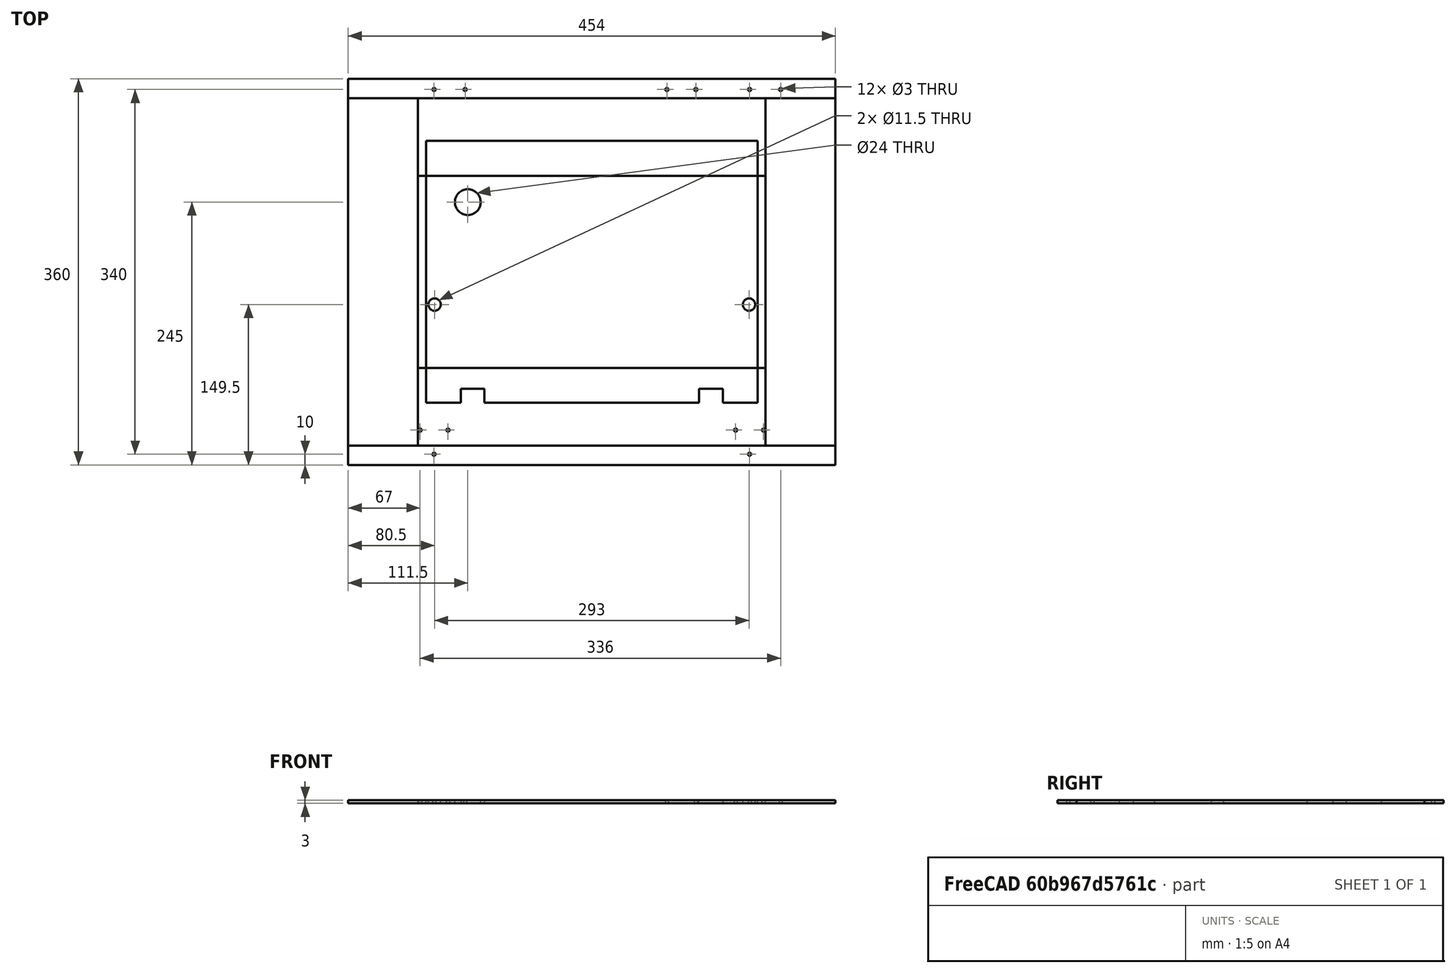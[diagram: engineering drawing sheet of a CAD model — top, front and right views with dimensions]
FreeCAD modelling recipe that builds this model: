
FCSTD DOCUMENT  (FreeCAD 0.19R24291 (Git))
Label: panel-drawing
License: Other
LicenseURL: GPL3
objects: TechDraw::DrawViewDimension×30, TechDraw::DrawViewAnnotation×9, Part::Feature×5, TechDraw::DrawSVGTemplate×5, TechDraw::DrawViewPart×5, TechDraw::DrawPage×5, Part::Part2DObjectPython×5
note: 10 computed .brp shape members not serialized (recipe doc carries the construction recipe); baked Part::Feature solids carry a one-line shape summary decoded from their .brp

FEATURE [Part::Feature] Box002001001  label="side-panel"
  shape: bbox 454 x 324 x 3 mm, 6 faces (baked)
FEATURE [Part::Feature] Cut008004003004014002002005003004003002003001003001002001002002011001007001001001001  label="rear-bottom"
  shape: bbox 309 x 244 x 3 mm, 14 faces (baked)
FEATURE [Part::Feature] Cut008004003004014002002005003004003002003001003001002001002002011001006001001001001001  label="rear-top"
  shape: bbox 324 x 179 x 3 mm, 9 faces (baked)
FEATURE [Part::Feature] Cut008004003004014002002005003004003002003001003001002001002002003004001001  label="front-panel"
  shape: bbox 454 x 360 x 3 mm, 18 faces (baked)
FEATURE [Part::Feature] Box002002001001001  label="top-panel"
  shape: bbox 324 x 324 x 3 mm, 6 faces (baked)
FEATURE [TechDraw::DrawSVGTemplate] Template
  EditableTexts = AuthorName=SnakeOil-XY; CheckDate=-; CreationDate=2022-01-24; DrawingNumber=1; FC-Scale=0.75; FC-Title=Rear-top panel; SheetNumber=1/1; Subtitle=3mm thick; SupervisorName=SnakeOil-XY; Weight=-
  Height = 297
  Orientation = 1
  Width = 420
FEATURE [TechDraw::DrawSVGTemplate] Template001
  EditableTexts = AuthorName=SnakeOil-XY; CheckDate=-; CreationDate=2022-01-24; DrawingNumber=1; FC-Scale=0.75; FC-Title=Rear-bottom panel; SheetNumber=1/1; Subtitle=3mm thick; SupervisorName=SnakeOil-XY; Weight=-
  Height = 297
  Orientation = 1
  Width = 420
FEATURE [TechDraw::DrawSVGTemplate] Template002
  EditableTexts = AuthorName=SnakeOil-XY; CheckDate=-; CreationDate=2022-01-24; DrawingNumber=1; FC-Scale=0.5; FC-Title=Top panel; SheetNumber=1/1; Subtitle=Top panel; SupervisorName=SnakeOil-XY; Weight=-
  Height = 297
  Orientation = 1
  Width = 420
FEATURE [TechDraw::DrawSVGTemplate] Template003
  EditableTexts = AuthorName=SnakeOil-XY; CheckDate=-; CreationDate=2022-01-24; DrawingNumber=1; FC-Scale=0.5; FC-Title=Side panel; SheetNumber=1/1; Subtitle=3mm; SupervisorName=SnakeOil-XY; Weight=-
  Height = 297
  Orientation = 1
  Width = 420
FEATURE [TechDraw::DrawSVGTemplate] Template004
  EditableTexts = AuthorName=SnakeOil-XY; CheckDate=-; CreationDate=2022-01-24; DrawingNumber=1; FC-Scale=0.5; FC-Title=Front panel; SheetNumber=1/1; Subtitle=3mm; SupervisorName=SnakeOil-XY; Weight=-
  Height = 297
  Orientation = 1
  Width = 420
FEATURE [TechDraw::DrawViewPart] View
  CoarseView = false
  Direction = (0,0,1)
  Focus = 100
  HardHidden = false
  IsoCount = 0
  IsoHidden = false
  IsoVisible = false
  LockPosition = false
  Perspective = false
  Rotation = 0
  Scale = 0.75
  ScaleType = 0
  SeamHidden = false
  SeamVisible = true
  SmoothHidden = false
  SmoothVisible = true
  Source = -> [Cut008004003004014002002005003004003002003001003001002001002002011001006001001001001001]
  X = 185.107
  XDirection = (1,0,0)
  Y = 185.41
FEATURE [TechDraw::DrawViewDimension] Dimension
  Arbitrary = false
  ArbitraryTolerances = false
  EqualTolerance = true
  FormatSpec = ⌀%.2f
  FormatSpecOverTolerance = %+.2f
  FormatSpecUnderTolerance = %+.2f
  Inverted = false
  LockPosition = false
  MeasureType = 1
  OverTolerance = 0
  References2D = -> [View]
  Rotation = 0
  ScaleType = 0
  TheoreticalExact = false
  Type = 5
  UnderTolerance = 0
  X = -63.1769
  Y = 37.7688
FEATURE [TechDraw::DrawViewDimension] Dimension001
  Arbitrary = false
  ArbitraryTolerances = false
  EqualTolerance = true
  FormatSpec = 2x ⌀%.2f
  FormatSpecOverTolerance = %+.2f
  FormatSpecUnderTolerance = %+.2f
  Inverted = false
  LockPosition = false
  MeasureType = 1
  OverTolerance = 0
  References2D = -> [View]
  Rotation = 0
  ScaleType = 0
  TheoreticalExact = false
  Type = 5
  UnderTolerance = 0
  X = -93.4041
  Y = -8.93294
FEATURE [TechDraw::DrawViewDimension] Dimension003
  Arbitrary = false
  ArbitraryTolerances = false
  EqualTolerance = true
  FormatSpec = %.2f
  FormatSpecOverTolerance = %+.2f
  FormatSpecUnderTolerance = %+.2f
  Inverted = false
  LockPosition = false
  MeasureType = 1
  OverTolerance = 0
  References2D = -> [View]
  Rotation = 0
  ScaleType = 0
  TheoreticalExact = false
  Type = 1
  UnderTolerance = 0
  X = -115.374
  Y = -31.5222
FEATURE [TechDraw::DrawViewDimension] Dimension005
  Arbitrary = false
  ArbitraryTolerances = false
  EqualTolerance = true
  FormatSpec = %.2f
  FormatSpecOverTolerance = %+.2f
  FormatSpecUnderTolerance = %+.2f
  Inverted = false
  LockPosition = false
  MeasureType = 1
  OverTolerance = 0
  References2D = -> [View]
  Rotation = 0
  ScaleType = 0
  TheoreticalExact = false
  Type = 2
  UnderTolerance = 0
  X = -93.2768
  Y = -42.6492
FEATURE [TechDraw::DrawViewDimension] Dimension007
  Arbitrary = false
  ArbitraryTolerances = false
  EqualTolerance = true
  FormatSpec = %.2f
  FormatSpecOverTolerance = %+.2f
  FormatSpecUnderTolerance = %+.2f
  Inverted = false
  LockPosition = false
  MeasureType = 1
  OverTolerance = 0
  References2D = -> [View]
  Rotation = 0
  ScaleType = 0
  TheoreticalExact = false
  Type = 1
  UnderTolerance = 0
  X = -102.965
  Y = 34.1163
FEATURE [TechDraw::DrawViewDimension] Dimension008
  Arbitrary = false
  ArbitraryTolerances = false
  EqualTolerance = true
  FormatSpec = %.2f
  FormatSpecOverTolerance = %+.2f
  FormatSpecUnderTolerance = %+.2f
  Inverted = false
  LockPosition = false
  MeasureType = 1
  OverTolerance = 0
  References2D = -> [View]
  Rotation = 0
  ScaleType = 0
  TheoreticalExact = false
  Type = 2
  UnderTolerance = 0
  X = -63.9426
  Y = 60.1316
FEATURE [TechDraw::DrawViewDimension] Dimension009
  Arbitrary = false
  ArbitraryTolerances = false
  EqualTolerance = true
  FormatSpec = %
  FormatSpecOverTolerance = %+.2f
  FormatSpecUnderTolerance = %+.2f
  Inverted = false
  LockPosition = false
  MeasureType = 1
  OverTolerance = 0
  References2D = -> [View]
  Rotation = 0
  ScaleType = 0
  TheoreticalExact = false
  Type = 1
  UnderTolerance = 0
  X = -2.19406
  Y = 79.8341
FEATURE [TechDraw::DrawViewDimension] Dimension010
  Arbitrary = false
  ArbitraryTolerances = false
  EqualTolerance = true
  FormatSpec = %.2f
  FormatSpecOverTolerance = %+.2f
  FormatSpecUnderTolerance = %+.2f
  Inverted = false
  LockPosition = false
  MeasureType = 1
  OverTolerance = 0
  References2D = -> [View]
  Rotation = 0
  ScaleType = 0
  TheoreticalExact = false
  Type = 2
  UnderTolerance = 0
  X = 143.441
  Y = 1.91196
FEATURE [TechDraw::DrawViewAnnotation] Annotation
  Font = osifont
  LineSpace = 80
  LockPosition = false
  MaxWidth = -1
  Rotation = 0
  ScaleType = 0
  Text = (394mm for 250 machine)
  TextSize = 5
  TextStyle = 0
  X = 219.271
  Y = 261.12
FEATURE [TechDraw::DrawPage] Page  label="rear-top-drawing"
  KeepUpdated = true
  NextBalloonIndex = 1
  ProjectionType = 0
  Template = -> Template
  Views = -> [View,Dimension,Dimension001,Dimension003,Dimension005,Dimension007,Dimension008,Dimension009,Dimension010,Annotation]
FEATURE [TechDraw::DrawViewPart] View001
  CoarseView = false
  Direction = (0,0,1)
  Focus = 100
  HardHidden = false
  IsoCount = 0
  IsoHidden = false
  IsoVisible = false
  LockPosition = false
  Perspective = false
  Rotation = 0
  Scale = 0.75
  ScaleType = 0
  SeamHidden = false
  SeamVisible = true
  SmoothHidden = false
  SmoothVisible = true
  Source = -> [Cut008004003004014002002005003004003002003001003001002001002002011001007001001001001]
  X = 164.19
  XDirection = (1,0,0)
  Y = 175.276
FEATURE [TechDraw::DrawViewDimension] Dimension011
  Arbitrary = false
  ArbitraryTolerances = false
  EqualTolerance = true
  FormatSpec = %.2f
  FormatSpecOverTolerance = %+.2f
  FormatSpecUnderTolerance = %+.2f
  Inverted = false
  LockPosition = false
  MeasureType = 1
  OverTolerance = 0
  References2D = -> [View001]
  Rotation = 0
  ScaleType = 0
  TheoreticalExact = false
  Type = 1
  UnderTolerance = 0
  X = -0.647751
  Y = 101.475
FEATURE [TechDraw::DrawViewDimension] Dimension012
  Arbitrary = false
  ArbitraryTolerances = false
  EqualTolerance = true
  FormatSpec = %.2f
  FormatSpecOverTolerance = %+.2f
  FormatSpecUnderTolerance = %+.2f
  Inverted = false
  LockPosition = false
  MeasureType = 1
  OverTolerance = 0
  References2D = -> [View001]
  Rotation = 0
  ScaleType = 0
  TheoreticalExact = false
  Type = 2
  UnderTolerance = 0
  X = 122.741
  Y = 0.12955
FEATURE [TechDraw::DrawViewDimension] Dimension013
  Arbitrary = false
  ArbitraryTolerances = false
  EqualTolerance = true
  FormatSpec = %.2f
  FormatSpecOverTolerance = %+.2f
  FormatSpecUnderTolerance = %+.2f
  Inverted = false
  LockPosition = false
  MeasureType = 1
  OverTolerance = 0
  References2D = -> [View001]
  Rotation = 0
  ScaleType = 0
  TheoreticalExact = false
  Type = 1
  UnderTolerance = 0
  X = -103.688
  Y = -91.5
FEATURE [TechDraw::DrawViewDimension] Dimension014
  Arbitrary = false
  ArbitraryTolerances = false
  EqualTolerance = true
  FormatSpec = %.2f
  FormatSpecOverTolerance = %+.2f
  FormatSpecUnderTolerance = %+.2f
  Inverted = false
  LockPosition = false
  MeasureType = 1
  OverTolerance = 0
  References2D = -> [View001]
  Rotation = 0
  ScaleType = 0
  TheoreticalExact = false
  Type = 1
  UnderTolerance = 0
  X = -83.25
  Y = -91.5
FEATURE [TechDraw::DrawViewDimension] Dimension015
  Arbitrary = false
  ArbitraryTolerances = false
  EqualTolerance = true
  FormatSpec = %.2f
  FormatSpecOverTolerance = %+.2f
  FormatSpecUnderTolerance = %+.2f
  Inverted = false
  LockPosition = false
  MeasureType = 1
  OverTolerance = 0
  References2D = -> [View001]
  Rotation = 0
  ScaleType = 0
  TheoreticalExact = false
  Type = 2
  UnderTolerance = 0
  X = -126.349
  Y = -83.6453
FEATURE [TechDraw::DrawViewAnnotation] Annotation001
  Font = osifont
  LineSpace = 80
  LockPosition = false
  MaxWidth = -1
  Rotation = 0
  ScaleType = 0
  Text = (379mm for 250 machine)
  TextSize = 5
  TextStyle = 0
  X = 199.659
  Y = 272.42
FEATURE [TechDraw::DrawViewAnnotation] Annotation002
  Font = osifont
  LineSpace = 80
  LockPosition = false
  MaxWidth = -1
  Rotation = 90
  ScaleType = 0
  Text = (294mm for 250 machine)
  TextSize = 5
  TextStyle = 0
  X = 287.979
  Y = 208.68
FEATURE [TechDraw::DrawPage] Page001  label="rear-bottom-drawing"
  KeepUpdated = true
  NextBalloonIndex = 1
  ProjectionType = 0
  Template = -> Template001
  Views = -> [View001,Dimension011,Dimension012,Dimension013,Dimension014,Dimension015,Annotation001,Annotation002]
FEATURE [TechDraw::DrawViewPart] View002
  CoarseView = false
  Direction = (0,0,1)
  Focus = 100
  HardHidden = false
  IsoCount = 0
  IsoHidden = false
  IsoVisible = false
  LockPosition = false
  Perspective = false
  Rotation = 0
  Scale = 0.5
  ScaleType = 0
  SeamHidden = false
  SeamVisible = true
  SmoothHidden = false
  SmoothVisible = true
  Source = -> [Box002002001001001]
  X = 119.638
  XDirection = (1,0,0)
  Y = 187.906
FEATURE [TechDraw::DrawViewDimension] Dimension016
  Arbitrary = false
  ArbitraryTolerances = false
  EqualTolerance = true
  FormatSpec = %.2f
  FormatSpecOverTolerance = %+.2f
  FormatSpecUnderTolerance = %+.2f
  Inverted = false
  LockPosition = false
  MeasureType = 1
  OverTolerance = 0
  References2D = -> [View002]
  Rotation = 0
  ScaleType = 0
  TheoreticalExact = false
  Type = 1
  UnderTolerance = 0
  X = -27.8551
  Y = -90.4707
FEATURE [TechDraw::DrawViewDimension] Dimension017
  Arbitrary = false
  ArbitraryTolerances = false
  EqualTolerance = true
  FormatSpec = %.2f
  FormatSpecOverTolerance = %+.2f
  FormatSpecUnderTolerance = %+.2f
  Inverted = false
  LockPosition = false
  MeasureType = 1
  OverTolerance = 0
  References2D = -> [View002]
  Rotation = 0
  ScaleType = 0
  TheoreticalExact = false
  Type = 2
  UnderTolerance = 0
  X = 97.3416
  Y = -29.3407
FEATURE [TechDraw::DrawViewAnnotation] Annotation003
  Font = osifont
  LineSpace = 80
  LockPosition = false
  MaxWidth = -1
  Rotation = 0
  ScaleType = 0
  Text = (394mm for 250 machine)
  TextSize = 5
  TextStyle = 0
  X = 127.92
  Y = 92.9756
FEATURE [TechDraw::DrawViewAnnotation] Annotation004
  Font = osifont
  LineSpace = 80
  LockPosition = false
  MaxWidth = -1
  Rotation = 90
  ScaleType = 0
  Text = (374mm for 250 machine)
  TextSize = 5
  TextStyle = 0
  X = 218.728
  Y = 192.14
FEATURE [TechDraw::DrawPage] Page002  label="top-drawing"
  KeepUpdated = true
  NextBalloonIndex = 1
  ProjectionType = 0
  Template = -> Template002
  Views = -> [View002,Dimension016,Dimension017,Annotation003,Annotation004]
FEATURE [TechDraw::DrawViewPart] View003
  CoarseView = false
  Direction = (0,0,1)
  Focus = 100
  HardHidden = false
  IsoCount = 0
  IsoHidden = false
  IsoVisible = false
  LockPosition = false
  Perspective = false
  Rotation = 0
  Scale = 0.5
  ScaleType = 0
  SeamHidden = false
  SeamVisible = true
  SmoothHidden = false
  SmoothVisible = true
  Source = -> [Box002001001]
  X = 168.552
  XDirection = (1,0,0)
  Y = 178.45
FEATURE [TechDraw::DrawViewDimension] Dimension018
  Arbitrary = false
  ArbitraryTolerances = false
  EqualTolerance = true
  FormatSpec = %.2f
  FormatSpecOverTolerance = %+.2f
  FormatSpecUnderTolerance = %+.2f
  Inverted = false
  LockPosition = false
  MeasureType = 1
  OverTolerance = 0
  References2D = -> [View003]
  Rotation = 0
  ScaleType = 0
  TheoreticalExact = false
  Type = 1
  UnderTolerance = 0
  X = -38.0811
  Y = -89.2997
FEATURE [TechDraw::DrawViewDimension] Dimension019
  Arbitrary = false
  ArbitraryTolerances = false
  EqualTolerance = true
  FormatSpec = %.2f
  FormatSpecOverTolerance = %+.2f
  FormatSpecUnderTolerance = %+.2f
  Inverted = false
  LockPosition = false
  MeasureType = 1
  OverTolerance = 0
  References2D = -> [View003]
  Rotation = 0
  ScaleType = 0
  TheoreticalExact = false
  Type = 2
  UnderTolerance = 0
  X = 121.067
  Y = -19.5288
FEATURE [TechDraw::DrawViewAnnotation] Annotation005
  Font = osifont
  LineSpace = 80
  LockPosition = false
  MaxWidth = -1
  Rotation = 0
  ScaleType = 0
  Text = (504mm for 250 machine)
  TextSize = 5
  TextStyle = 0
  X = 167.525
  Y = 84.7874
FEATURE [TechDraw::DrawViewAnnotation] Annotation006
  Font = osifont
  LineSpace = 80
  LockPosition = false
  MaxWidth = -1
  Rotation = 90
  ScaleType = 0
  Text = (374mm for 250 machine)
  TextSize = 5
  TextStyle = 0
  X = 291.777
  Y = 192.928
FEATURE [TechDraw::DrawPage] Page003  label="side-drawing"
  KeepUpdated = true
  NextBalloonIndex = 1
  ProjectionType = 0
  Template = -> Template003
  Views = -> [View003,Dimension018,Dimension019,Annotation005,Annotation006]
FEATURE [TechDraw::DrawViewPart] View004
  CoarseView = false
  Direction = (0,0,1)
  Focus = 100
  HardHidden = false
  IsoCount = 0
  IsoHidden = false
  IsoVisible = false
  LockPosition = false
  Perspective = false
  Rotation = 0
  Scale = 0.5
  ScaleType = 0
  SeamHidden = false
  SeamVisible = true
  SmoothHidden = false
  SmoothVisible = true
  Source = -> [Cut008004003004014002002005003004003002003001003001002001002002003004001001]
  X = 151.176
  XDirection = (1,0,0)
  Y = 183.76
FEATURE [TechDraw::DrawViewDimension] Dimension020
  Arbitrary = false
  ArbitraryTolerances = false
  EqualTolerance = true
  FormatSpec = %.2f
  FormatSpecOverTolerance = %+.2f
  FormatSpecUnderTolerance = %+.2f
  Inverted = false
  LockPosition = false
  MeasureType = 1
  OverTolerance = 0
  References2D = -> [View004]
  Rotation = 0
  ScaleType = 0
  TheoreticalExact = false
  Type = 1
  UnderTolerance = 0
  X = -31.6164
  Y = -105.298
FEATURE [TechDraw::DrawViewDimension] Dimension021
  Arbitrary = false
  ArbitraryTolerances = false
  EqualTolerance = true
  FormatSpec = %.2f
  FormatSpecOverTolerance = %+.2f
  FormatSpecUnderTolerance = %+.2f
  Inverted = false
  LockPosition = false
  MeasureType = 1
  OverTolerance = 0
  References2D = -> [View004]
  Rotation = 0
  ScaleType = 0
  TheoreticalExact = false
  Type = 2
  UnderTolerance = 0
  X = 121.807
  Y = -27.4284
FEATURE [TechDraw::DrawViewDimension] Dimension022
  Arbitrary = false
  ArbitraryTolerances = false
  EqualTolerance = true
  FormatSpec = %.2f
  FormatSpecOverTolerance = %+.2f
  FormatSpecUnderTolerance = %+.2f
  Inverted = false
  LockPosition = false
  MeasureType = 1
  OverTolerance = 0
  References2D = -> [View004]
  Rotation = 0
  ScaleType = 0
  TheoreticalExact = false
  Type = 1
  UnderTolerance = 0
  X = -93.5568
  Y = 101.636
FEATURE [TechDraw::DrawViewDimension] Dimension023
  Arbitrary = false
  ArbitraryTolerances = false
  EqualTolerance = true
  FormatSpec = %.2f
  FormatSpecOverTolerance = %+.2f
  FormatSpecUnderTolerance = %+.2f
  Inverted = false
  LockPosition = false
  MeasureType = 1
  OverTolerance = 0
  References2D = -> [View004]
  Rotation = 0
  ScaleType = 0
  TheoreticalExact = false
  Type = 1
  UnderTolerance = 0
  X = -65.7958
  Y = 101.577
FEATURE [TechDraw::DrawViewDimension] Dimension024
  Arbitrary = false
  ArbitraryTolerances = false
  EqualTolerance = true
  FormatSpec = %.2f
  FormatSpecOverTolerance = %+.2f
  FormatSpecUnderTolerance = %+.2f
  Inverted = false
  LockPosition = false
  MeasureType = 1
  OverTolerance = 0
  References2D = -> [View004]
  Rotation = 0
  ScaleType = 0
  TheoreticalExact = false
  Type = 1
  UnderTolerance = 0
  X = 79.383
  Y = 100.436
FEATURE [TechDraw::DrawViewDimension] Dimension025
  Arbitrary = false
  ArbitraryTolerances = false
  EqualTolerance = true
  FormatSpec = %.2f
  FormatSpecOverTolerance = %+.2f
  FormatSpecUnderTolerance = %+.2f
  Inverted = false
  LockPosition = false
  MeasureType = 1
  OverTolerance = 0
  References2D = -> [View004]
  Rotation = 0
  ScaleType = 0
  TheoreticalExact = false
  Type = 1
  UnderTolerance = 0
  X = 41.3147
  Y = 100.423
FEATURE [TechDraw::DrawViewDimension] Dimension026
  Arbitrary = false
  ArbitraryTolerances = false
  EqualTolerance = true
  FormatSpec = %.2f
  FormatSpecOverTolerance = %+.2f
  FormatSpecUnderTolerance = %+.2f
  Inverted = false
  LockPosition = false
  MeasureType = 1
  OverTolerance = 0
  References2D = -> [View004]
  Rotation = 0
  ScaleType = 0
  TheoreticalExact = false
  Type = 2
  UnderTolerance = 0
  X = -129.096
  Y = 89.8844
FEATURE [TechDraw::DrawViewDimension] Dimension027
  Arbitrary = false
  ArbitraryTolerances = false
  EqualTolerance = true
  FormatSpec = %.2f
  FormatSpecOverTolerance = %+.2f
  FormatSpecUnderTolerance = %+.2f
  Inverted = false
  LockPosition = false
  MeasureType = 1
  OverTolerance = 0
  References2D = -> [View004]
  Rotation = 0
  ScaleType = 0
  TheoreticalExact = false
  Type = 1
  UnderTolerance = 0
  X = -96.3022
  Y = -61.0088
FEATURE [TechDraw::DrawViewDimension] Dimension028
  Arbitrary = false
  ArbitraryTolerances = false
  EqualTolerance = true
  FormatSpec = %.2f
  FormatSpecOverTolerance = %+.2f
  FormatSpecUnderTolerance = %+.2f
  Inverted = false
  LockPosition = false
  MeasureType = 1
  OverTolerance = 0
  References2D = -> [View004]
  Rotation = 0
  ScaleType = 0
  TheoreticalExact = false
  Type = 1
  UnderTolerance = 0
  X = -96.2754
  Y = -91.6838
FEATURE [TechDraw::DrawViewDimension] Dimension029
  Arbitrary = false
  ArbitraryTolerances = false
  EqualTolerance = true
  FormatSpec = %.2f
  FormatSpecOverTolerance = %+.2f
  FormatSpecUnderTolerance = %+.2f
  Inverted = false
  LockPosition = false
  MeasureType = 1
  OverTolerance = 0
  References2D = -> [View004]
  Rotation = 0
  ScaleType = 0
  TheoreticalExact = false
  Type = 1
  UnderTolerance = 0
  X = -90.4931
  Y = -99.587
FEATURE [TechDraw::DrawViewDimension] Dimension030
  Arbitrary = false
  ArbitraryTolerances = false
  EqualTolerance = true
  FormatSpec = %.2f
  FormatSpecOverTolerance = %+.2f
  FormatSpecUnderTolerance = %+.2f
  Inverted = false
  LockPosition = false
  MeasureType = 1
  OverTolerance = 0
  References2D = -> [View004]
  Rotation = 0
  ScaleType = 0
  TheoreticalExact = false
  Type = 2
  UnderTolerance = 0
  X = -58.819
  Y = -76.9697
FEATURE [TechDraw::DrawViewDimension] Dimension031
  Arbitrary = false
  ArbitraryTolerances = false
  EqualTolerance = true
  FormatSpec = %.2f
  FormatSpecOverTolerance = %+.2f
  FormatSpecUnderTolerance = %+.2f
  Inverted = false
  LockPosition = false
  MeasureType = 1
  OverTolerance = 0
  References2D = -> [View004]
  Rotation = 0
  ScaleType = 0
  TheoreticalExact = false
  Type = 2
  UnderTolerance = 0
  X = -50.4742
  Y = -59.6006
FEATURE [TechDraw::DrawViewDimension] Dimension032
  Arbitrary = false
  ArbitraryTolerances = false
  EqualTolerance = true
  FormatSpec = 12x ⌀%.2f
  FormatSpecOverTolerance = %+.2f
  FormatSpecUnderTolerance = %+.2f
  Inverted = false
  LockPosition = false
  MeasureType = 1
  OverTolerance = 0
  References2D = -> [View004]
  Rotation = 0
  ScaleType = 0
  TheoreticalExact = false
  Type = 5
  UnderTolerance = 0
  X = 38.1332
  Y = -54.992
FEATURE [TechDraw::DrawViewAnnotation] Annotation007
  Font = osifont
  LineSpace = 80
  LockPosition = false
  MaxWidth = -1
  Rotation = 90
  ScaleType = 0
  Text = (430mm for 250 machine)
  TextSize = 5
  TextStyle = 0
  X = 275.299
  Y = 189.185
FEATURE [TechDraw::DrawViewAnnotation] Annotation008
  Font = osifont
  LineSpace = 80
  LockPosition = false
  MaxWidth = -1
  Rotation = 0
  ScaleType = 0
  Text = (504mm for 250 machine)
  TextSize = 5
  TextStyle = 0
  X = 155.686
  Y = 74.25
FEATURE [TechDraw::DrawPage] Page004  label="front-drawing"
  KeepUpdated = true
  NextBalloonIndex = 1
  ProjectionType = 0
  Template = -> Template004
  Views = -> [View004,Dimension020,Dimension021,Dimension022,Dimension023,Dimension024,Dimension025,Dimension026,Dimension027,Dimension028,Dimension029,Dimension030,Dimension031,Dimension032,Annotation007,Annotation008]
FEATURE [Part::Part2DObjectPython] Shape2DView  label="side-panel-2d"  # Draft 2D object (typed FeaturePython)
  Base = -> Box002001001
  FuseArch = false
  HiddenLines = false
  InPlace = true
  Projection = (0,0,1)
  ProjectionMode = 0
  SegmentLength = 0.05
  Tessellation = false
  VisibleOnly = false
FEATURE [Part::Part2DObjectPython] Shape2DView001  label="rear-bottom-2d"  # Draft 2D object (typed FeaturePython)
  Base = -> Cut008004003004014002002005003004003002003001003001002001002002011001007001001001001
  FuseArch = false
  HiddenLines = false
  InPlace = true
  Projection = (0,0,1)
  ProjectionMode = 0
  SegmentLength = 0.05
  Tessellation = false
  VisibleOnly = false
FEATURE [Part::Part2DObjectPython] Shape2DView002  label="rear-top-2d"  # Draft 2D object (typed FeaturePython)
  Base = -> Cut008004003004014002002005003004003002003001003001002001002002011001006001001001001001
  FaceNumbers = [2]
  FuseArch = false
  HiddenLines = false
  InPlace = true
  Projection = (0,0,1)
  ProjectionMode = 0
  SegmentLength = 0.05
  Tessellation = false
  VisibleOnly = false
FEATURE [Part::Part2DObjectPython] Shape2DView003  label="front-panel-2d"  # Draft 2D object (typed FeaturePython)
  Base = -> Cut008004003004014002002005003004003002003001003001002001002002003004001001
  FuseArch = false
  HiddenLines = false
  InPlace = true
  Projection = (0,0,1)
  ProjectionMode = 0
  SegmentLength = 0.05
  Tessellation = false
  VisibleOnly = false
FEATURE [Part::Part2DObjectPython] Shape2DView004  label="top-panel-2d"  # Draft 2D object (typed FeaturePython)
  Base = -> Box002002001001001
  FaceNumbers = [5]
  FuseArch = false
  HiddenLines = false
  InPlace = true
  Projection = (0,0,1)
  ProjectionMode = 0
  SegmentLength = 0.05
  Tessellation = false
  VisibleOnly = false
